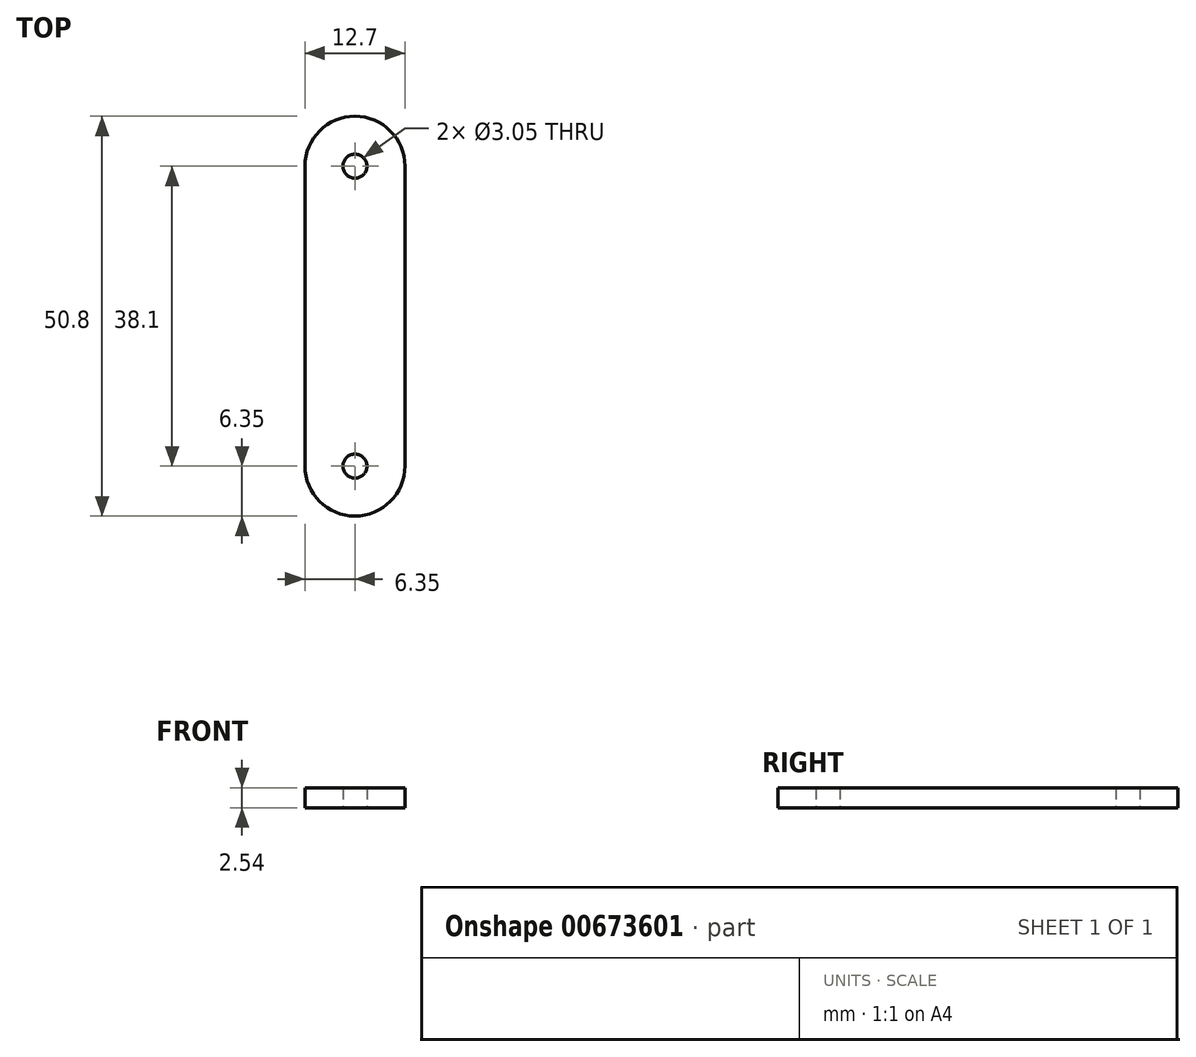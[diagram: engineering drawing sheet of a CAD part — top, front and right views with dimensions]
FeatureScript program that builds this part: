
annotation { "Feature Type Name" : "Feature", "Feature Type Description" : "" }
export const myFeature = defineFeature(function(context is Context, id is Id, definition is map)
    precondition{}
    {
        {
            var Q0;
            Q0=qCreatedBy(makeId("Top.planeOp"),FACE);
            var sketch = newSketch(context, id + "F0", { "sketchPlane" : qUnion([Q0])});
            skLineSegment(sketch, "E0.bottom", {"start": v(0, 25.4) * mm, "end": v(0, 25.4) * mm});
            skLineSegment(sketch, "E0.top", {"start": v(0, -25.4) * mm, "end": v(0, -25.4) * mm});
            skLineSegment(sketch, "E0.left", {"start": v(6.35, 19.05) * mm, "end": v(6.35, -19.05) * mm});
            skLineSegment(sketch, "E0.right", {"start": v(-6.35, 19.05) * mm, "end": v(-6.35, -19.05) * mm});
            skPoint(sketch, "E0.middle", {"position": v(0, 0) * mm});
            skPoint(sketch, "E1.visualSharp", {"position": v(-6.35, 25.4) * mm});
            skArc(sketch, "E1.filletArc", {"start": v(0, 25.4) * mm, "mid": v(-4.5, 23.54) * mm, "end": v(-6.35, 19.05) * mm});
            skPoint(sketch, "E2.visualSharp", {"position": v(6.35, 25.4) * mm});
            skArc(sketch, "E2.filletArc", {"start": v(6.35, 19.05) * mm, "mid": v(4.5, 23.54) * mm, "end": v(0, 25.4) * mm});
            skPoint(sketch, "E3.visualSharp", {"position": v(-6.35, -25.4) * mm});
            skArc(sketch, "E3.filletArc", {"start": v(-6.35, -19.05) * mm, "mid": v(-4.5, -23.54) * mm, "end": v(0, -25.4) * mm});
            skPoint(sketch, "E4.visualSharp", {"position": v(6.35, -25.4) * mm});
            skArc(sketch, "E4.filletArc", {"start": v(0, -25.4) * mm, "mid": v(4.5, -23.54) * mm, "end": v(6.35, -19.05) * mm});
            skCircle(sketch, "E5", {"center": v(0, -19.05) * mm, "radius": 1.52 * mm});
            skCircle(sketch, "E6", {"center": v(0, 19.05) * mm, "radius": 1.52 * mm});
            skSolve(sketch);
        }
        {
            var Q0;
            Q0=makeQuery(id+"F0.imprint","IMPRINT",FACE,{"disambiguationData":[TD([[makeQuery(id+"F0.imprint","IMPRINT",EDGE,{"derivedFrom":sQuery(id+"F0.wireOp",EDGE,"E0.left")}),-1.0]])]});
            extrude(context, id + "F1", {"entities" : qUnion([Q0]), "depth" : 2.54 * mm});
        }
    });
